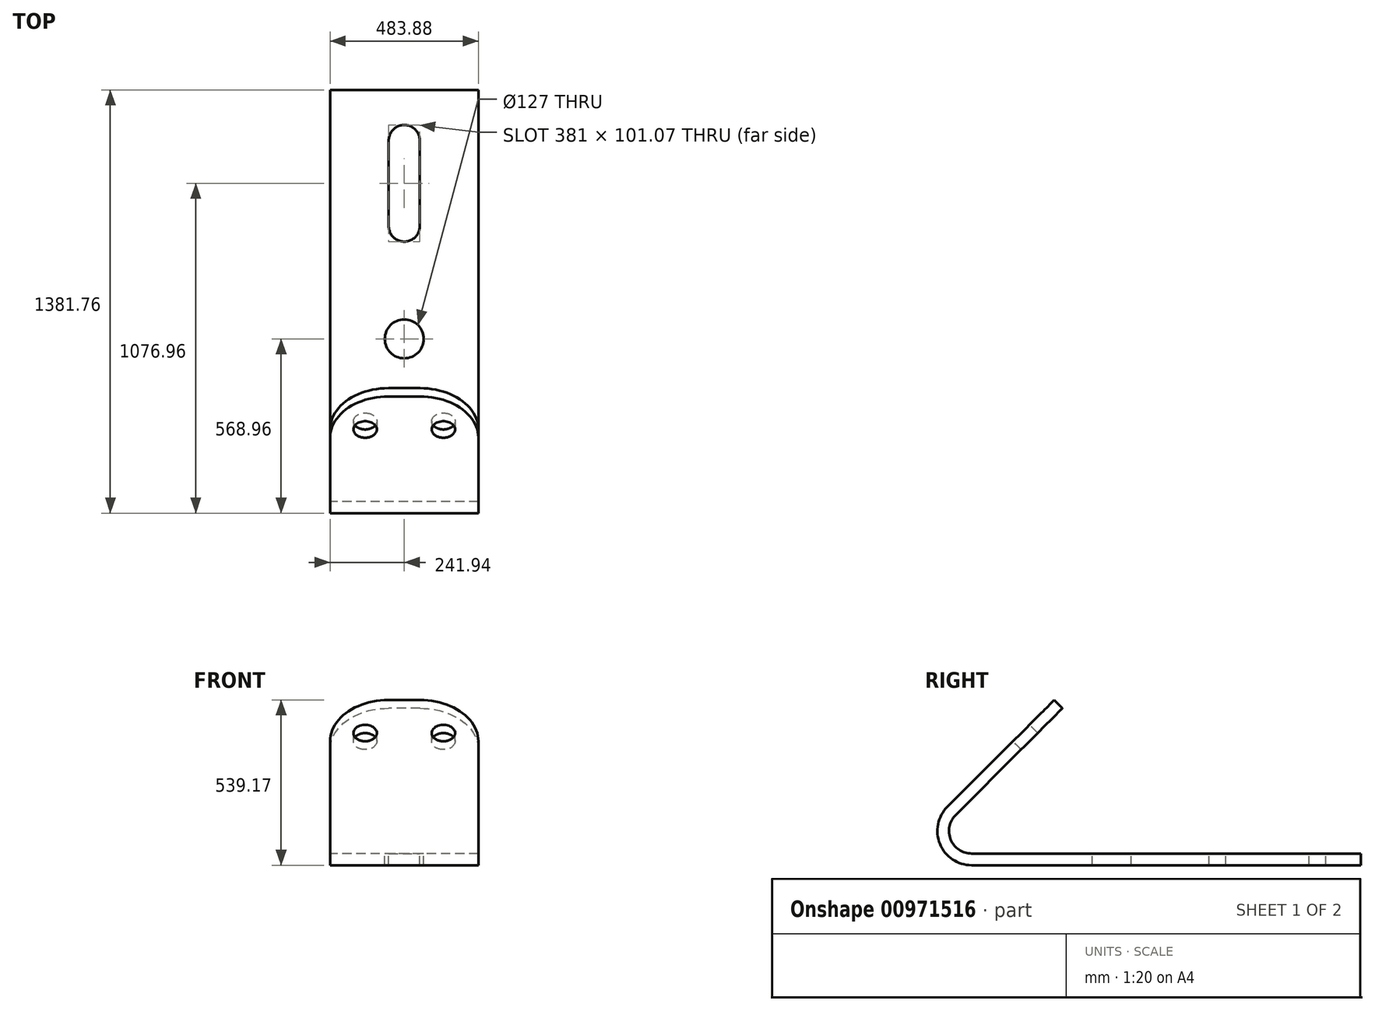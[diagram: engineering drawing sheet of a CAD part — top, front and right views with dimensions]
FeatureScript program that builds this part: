
annotation { "Feature Type Name" : "Feature", "Feature Type Description" : "" }
export const myFeature = defineFeature(function(context is Context, id is Id, definition is map)
    precondition{}
    {
        {
            var Q0;
            Q0=qCreatedBy(makeId("Right.planeOp"),FACE);
            var sketch = newSketch(context, id + "F0", { "sketchPlane" : qUnion([Q0])});
            skLineSegment(sketch, "E0.top", {"start": v(1270, 0) * mm, "end": v(0, 0) * mm});
            skLineSegment(sketch, "E1", {"start": v(269.36, 539.17) * mm, "end": v(-79.03, 190.79) * mm});
            skPoint(sketch, "E2.orphan", {"position": v(-64.8, 0) * mm});
            skPoint(sketch, "E3.visualSharp", {"position": v(-422.8, -48.26) * mm});
            skPoint(sketch, "E4.visualSharp", {"position": v(-269.81, 0) * mm});
            skArc(sketch, "E4.filletArc", {"start": v(-79.03, 190.79) * mm, "mid": v(-103.25, 69) * mm, "end": v(0, 0) * mm});
            skLineSegment(sketch, "E5.0", {"start": v(296.3, 512.23) * mm, "end": v(-52.09, 163.85) * mm});
            skArc(sketch, "E5.1", {"start": v(-52.09, 163.85) * mm, "mid": v(-68.05, 83.57) * mm, "end": v(0, 38.1) * mm});
            skLineSegment(sketch, "E5.2", {"start": v(1270, 38.1) * mm, "end": v(0, 38.1) * mm});
            skLineSegment(sketch, "E6", {"start": v(269.36, 539.17) * mm, "end": v(296.3, 512.23) * mm});
            skLineSegment(sketch, "E7", {"start": v(1270, 38.1) * mm, "end": v(1270, 0) * mm});
            skSolve(sketch);
        }
        {
            var Q0;
            Q0 = qSketchRegion(id + "F0", true);
            extrude(context, id + "F1", {"entities" : qUnion([Q0]), "endBound" : BoundingType.SYMMETRIC, "depth" : 483.87 * mm, "offsetDistance" : 25.4 * mm});
        }
        {
            var Q0;
            Q0=makeQuery(id+"F1.opExtrude","SWEPT_FACE",FACE,{"disambiguationData":[OSD([sQuery(id+"F0.wireOp",EDGE,"E1")])]});
            var sketch = newSketch(context, id + "F2", { "sketchPlane" : qUnion([Q0])});
            skLineSegment(sketch, "E8", {"start": v(0, 571.72) * mm, "end": v(0, -193.53) * mm, "construction": true});
            skCircle(sketch, "E9", {"center": v(-127.64, 419.24) * mm, "radius": 38.1 * mm});
            skCircle(sketch, "E10.MirrorC", {"center": v(127.63, 419.24) * mm, "radius": 38.1 * mm});
            skSolve(sketch);
        }
        {
            var Q0;
            Q0 = qSketchRegion(id + "F2", true);
            extrude(context, id + "F3", {"entities" : qUnion([Q0]), "operationType" : NewBodyOperationType.REMOVE, "endBound" : BoundingType.UP_TO_NEXT, "oppositeDirection" : true, "depth" : 25.4 * mm, "offsetDistance" : 25.4 * mm});
        }
        {
            var Q0;
            Q0=makeQuery(id+"F1.opExtrude","SWEPT_FACE",FACE,{"disambiguationData":[OSD([sQuery(id+"F0.wireOp",EDGE,"E5.2")])]});
            var sketch = newSketch(context, id + "F4", { "sketchPlane" : qUnion([Q0])});
            skLineSegment(sketch, "E11", {"start": v(0, 1270) * mm, "end": v(0, 0) * mm, "construction": true});
            skCircle(sketch, "E12", {"center": v(0, 457.2) * mm, "radius": 63.5 * mm});
            skArc(sketch, "E13", {"start": v(-50.53, 829.5) * mm, "mid": v(0, 774.7) * mm, "end": v(50.53, 829.5) * mm});
            skArc(sketch, "E14.MirrorC", {"start": v(50.53, 829.5) * mm, "mid": v(0, 774.7) * mm, "end": v(-50.53, 829.5) * mm});
            skArc(sketch, "E15", {"start": v(50.53, 1100.9) * mm, "mid": v(0, 1155.7) * mm, "end": v(-50.53, 1100.9) * mm});
            skLineSegment(sketch, "E16", {"start": v(-50.53, 829.5) * mm, "end": v(-50.53, 1100.9) * mm});
            skLineSegment(sketch, "E17.MirrorCS", {"start": v(50.53, 829.5) * mm, "end": v(50.53, 1100.9) * mm});
            skSolve(sketch);
        }
        {
            var Q0;
            Q0 = qSketchRegion(id + "F4", true);
            extrude(context, id + "F5", {"entities" : qUnion([Q0]), "operationType" : NewBodyOperationType.REMOVE, "endBound" : BoundingType.UP_TO_NEXT, "oppositeDirection" : true, "depth" : 25.4 * mm, "offsetDistance" : 25.4 * mm});
        }
        {
            var Q0;
            Q0=makeQuery(id+"F1.opExtrude","CAP_EDGE",EDGE,{"disambiguationData":[OSD([sQuery(id+"F0.wireOp",EDGE,"E6")])],"isStart":true});
            var Q1;
            Q1=makeQuery(id+"F1.opExtrude","CAP_EDGE",EDGE,{"disambiguationData":[OSD([sQuery(id+"F0.wireOp",EDGE,"E6")])],"isStart":false});
            fillet(context, id + "F6", {"entities" : qUnion([Q0, Q1]), "radius" : 190.5 * mm, "tangentPropagation" : true, "allowEdgeOverflow" : false});
        }
    });
